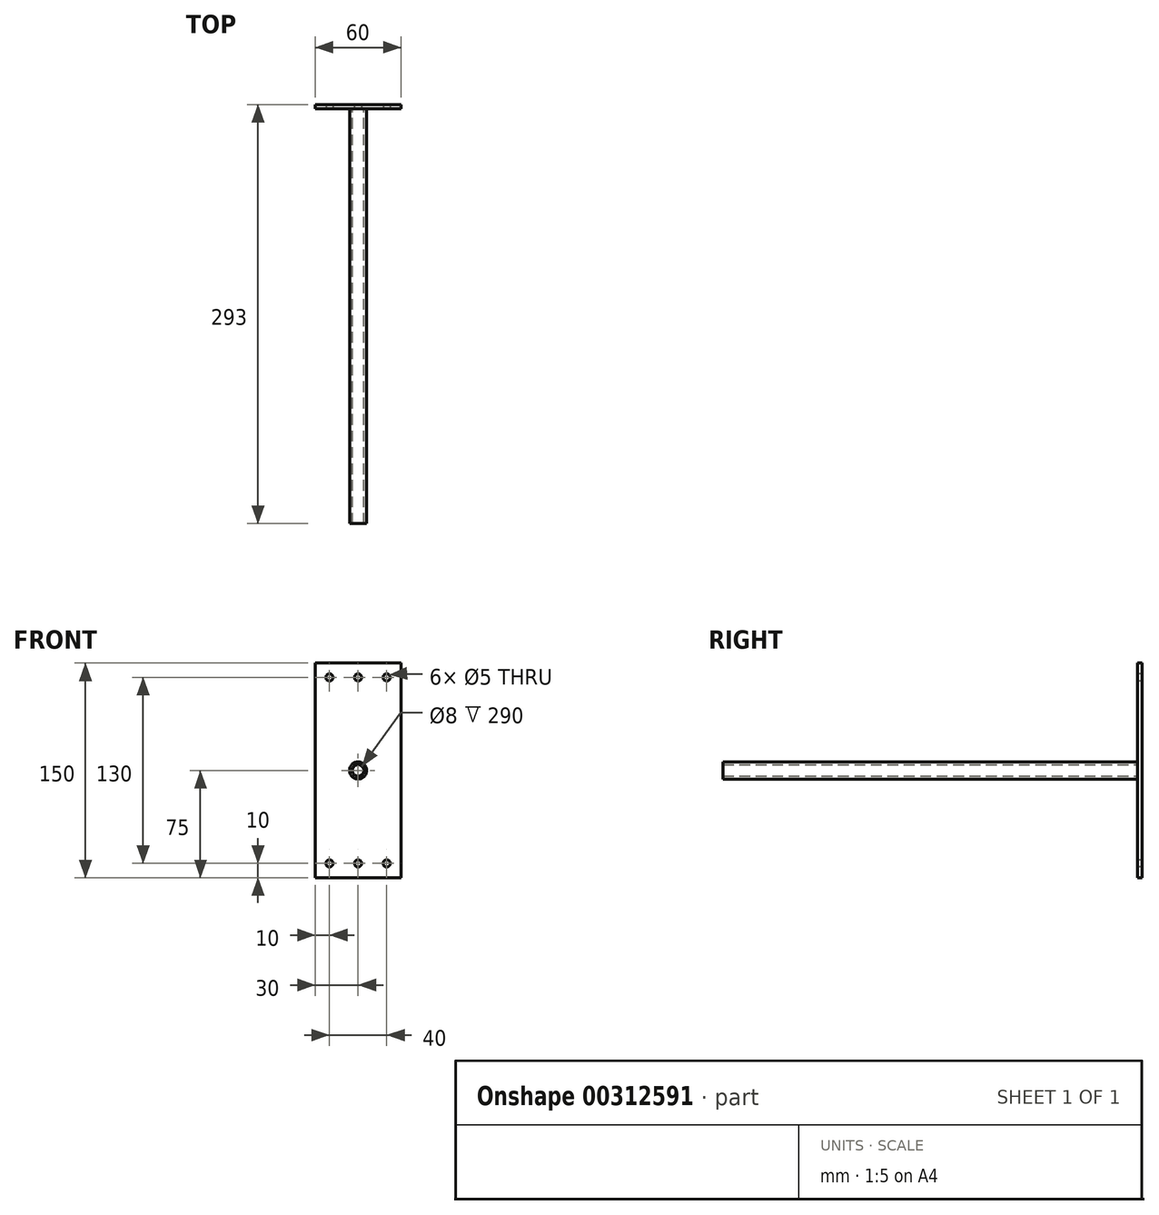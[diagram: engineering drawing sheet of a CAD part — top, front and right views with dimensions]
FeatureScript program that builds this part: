
annotation { "Feature Type Name" : "Feature", "Feature Type Description" : "" }
export const myFeature = defineFeature(function(context is Context, id is Id, definition is map)
    precondition{}
    {
        {
            var Q0;
            Q0=qCreatedBy(makeId("Front.planeOp"),FACE);
            var sketch = newSketch(context, id + "F0", { "sketchPlane" : qUnion([Q0])});
            skLineSegment(sketch, "E0.bottom", {"start": v(-30, 75) * mm, "end": v(30, 75) * mm});
            skLineSegment(sketch, "E0.top", {"start": v(-30, -75) * mm, "end": v(30, -75) * mm});
            skLineSegment(sketch, "E0.left", {"start": v(-30, 75) * mm, "end": v(-30, -75) * mm});
            skLineSegment(sketch, "E0.right", {"start": v(30, 75) * mm, "end": v(30, -75) * mm});
            skPoint(sketch, "E1", {"position": v(0, 75) * mm});
            skPoint(sketch, "E2", {"position": v(30, 0) * mm});
            skSolve(sketch);
        }
        {
            var Q0;
            Q0=makeQuery(id+"F0.imprint","IMPRINT",FACE,{"disambiguationData":[TD([[makeQuery(id+"F0.imprint","IMPRINT",EDGE,{"derivedFrom":sQuery(id+"F0.wireOp",EDGE,"E0.bottom")}),-1.0]])]});
            extrude(context, id + "F1", {"entities" : qUnion([Q0]), "depth" : 3 * mm});
        }
        {
            var Q0;
            Q0=makeQuery(id+"F1.opExtrude","CAP_FACE",FACE,{"disambiguationData":[OSD([sQuery(id+"F0.wireOp",EDGE,"E0.bottom"),sQuery(id+"F0.wireOp",EDGE,"E0.top"),sQuery(id+"F0.wireOp",EDGE,"E0.left"),sQuery(id+"F0.wireOp",EDGE,"E0.right")])],"isStart":false});
            var sketch = newSketch(context, id + "F2", { "sketchPlane" : qUnion([Q0])});
            skCircle(sketch, "E3", {"center": v(0, 0) * mm, "radius": 6 * mm});
            skCircle(sketch, "E4.0", {"center": v(0, 0) * mm, "radius": 4 * mm});
            skSolve(sketch);
        }
        {
            var Q0;
            Q0 = qSketchRegion(id + "F2", true);
            extrude(context, id + "F3", {"entities" : qUnion([Q0]), "operationType" : NewBodyOperationType.ADD, "depth" : 290 * mm});
        }
        {
            var Q0;
            {var subQ0=sQuery(id+"F0.wireOp",EDGE,"E0.left");var subQ1=sQuery(id+"F0.wireOp",EDGE,"E0.top");var subQ2=sQuery(id+"F0.wireOp",EDGE,"E0.right");var subQ3=sQuery(id+"F0.wireOp",EDGE,"E0.bottom");Q0=makeQuery(id+"F3.boolean.opBoolean","SPLIT",FACE,{"disambiguationData":[TD([makeQuery(id+"F1.opExtrude","SWEPT_FACE",FACE,{"disambiguationData":[OSD([subQ3])]})])],"derivedFrom":makeQuery(id+"F1.opExtrude","CAP_FACE",FACE,{"disambiguationData":[OSD([subQ3,subQ1,subQ0,subQ2])],"isStart":false})});}
            var sketch = newSketch(context, id + "F4", { "sketchPlane" : qUnion([Q0])});
            skPoint(sketch, "E5", {"position": v(-20, 65) * mm});
            skPoint(sketch, "E6", {"position": v(20, 65) * mm});
            skPoint(sketch, "E7", {"position": v(-20, -65) * mm});
            skPoint(sketch, "E8", {"position": v(20, -65) * mm});
            skPoint(sketch, "E9", {"position": v(0, 65) * mm});
            skPoint(sketch, "E10", {"position": v(0, -65) * mm});
            skSolve(sketch);
        }
        {
            var Q0;
            Q0=sQuery(id+"F4.wireOp",VERTEX,"E5");
            var Q1;
            Q1=sQuery(id+"F4.wireOp",VERTEX,"E9");
            var Q2;
            Q2=sQuery(id+"F4.wireOp",VERTEX,"E6");
            var Q3;
            Q3=sQuery(id+"F4.wireOp",VERTEX,"E8");
            var Q4;
            Q4=sQuery(id+"F4.wireOp",VERTEX,"E10");
            var Q5;
            Q5=sQuery(id+"F4.wireOp",VERTEX,"E7");
            var Q6;
            Q6=makeQuery(id+"F1.opExtrude","SWEPT_BODY",BODY,{"disambiguationData":[OSD([sQuery(id+"F0.wireOp",EDGE,"E0.bottom"),sQuery(id+"F0.wireOp",EDGE,"E0.top"),sQuery(id+"F0.wireOp",EDGE,"E0.left"),sQuery(id+"F0.wireOp",EDGE,"E0.right")])]});
            hole(context, id + "F5", {"style" : HoleStyle.SIMPLE, "endStyle" : HoleEndStyle.THROUGH, "holeDiameter" : 5 * mm, "tappedDepth" : 12 * mm, "tapClearance" : 3, "locations" : qUnion([Q0, Q1, Q2, Q3, Q4, Q5]), "scope" : qUnion([Q6])});
        }
    });
